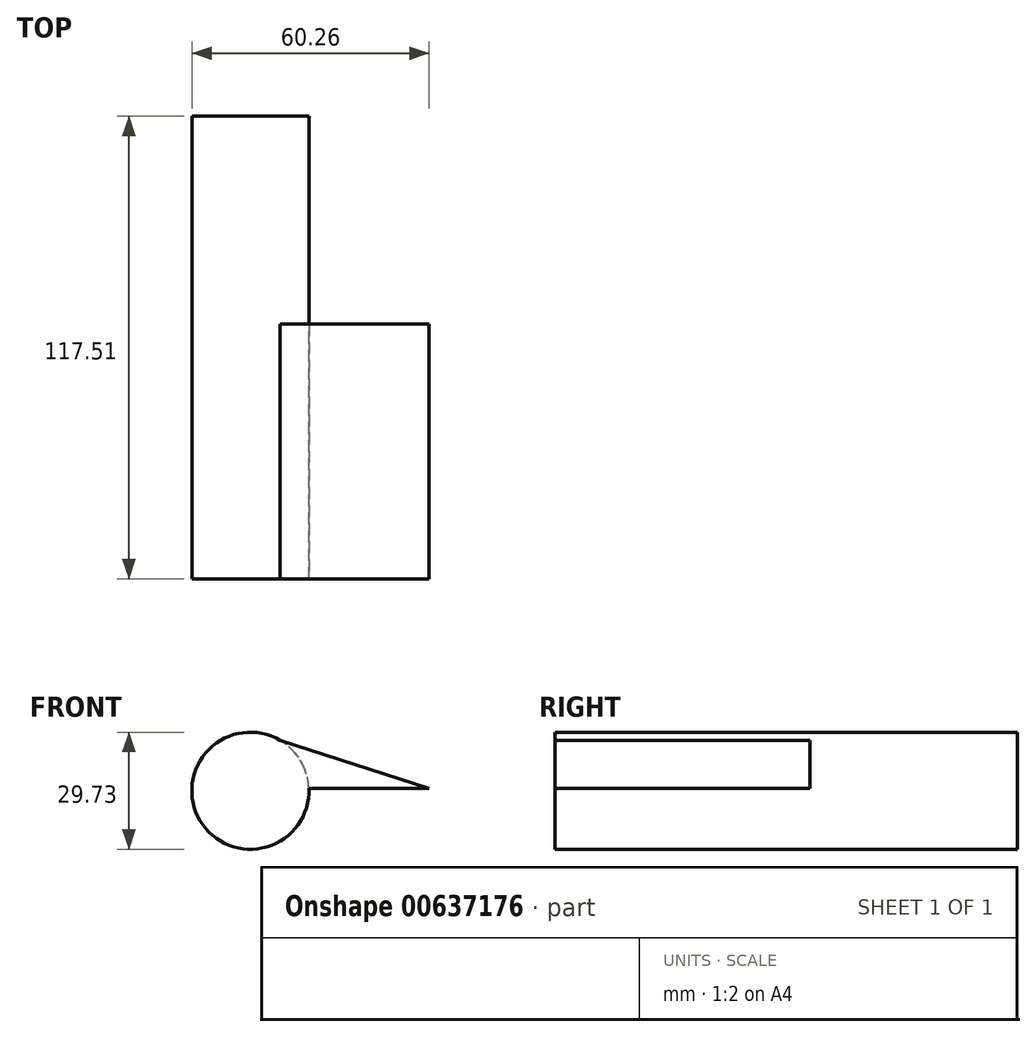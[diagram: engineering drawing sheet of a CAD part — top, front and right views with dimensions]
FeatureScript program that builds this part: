
annotation { "Feature Type Name" : "Feature", "Feature Type Description" : "" }
export const myFeature = defineFeature(function(context is Context, id is Id, definition is map)
    precondition{}
    {
        {
            var Q0;
            Q0=qCreatedBy(makeId("Front.planeOp"),FACE);
            var sketch = newSketch(context, id + "F0", { "sketchPlane" : qUnion([Q0])});
            skCircle(sketch, "E0", {"center": v(-0.34, -0.59) * mm, "radius": 14.87 * mm});
            skPoint(sketch, "E0.first.point", {"position": v(14.51, 0) * mm});
            skPoint(sketch, "E0.second.point", {"position": v(-15.2, 0) * mm});
            skPoint(sketch, "E0.third.point", {"position": v(0, 14.28) * mm});
            skSolve(sketch);
        }
        {
            var Q0;
            Q0=makeQuery(id+"F0.imprint","IMPRINT",FACE,{"disambiguationData":[TD([[makeQuery(id+"F0.imprint","IMPRINT",EDGE,{"derivedFrom":sQuery(id+"F0.wireOp",EDGE,"E0")}),1.0]])]});
            extrude(context, id + "F1", {"entities" : qUnion([Q0]), "depth" : 63.81 * mm, "offsetDistance" : 25.4 * mm});
        }
        {
            var Q0;
            Q0=makeQuery(id+"F1.opExtrude","CAP_FACE",FACE,{"disambiguationData":[OSD([sQuery(id+"F0.wireOp",EDGE,"E0")])],"isStart":true});
            extrude(context, id + "F2", {"entities" : qUnion([Q0]), "operationType" : NewBodyOperationType.ADD, "depth" : 53.7 * mm, "offsetDistance" : 25.4 * mm});
        }
        {
            var Q0;
            Q0=makeQuery(id+"F1.opExtrude","CAP_FACE",FACE,{"disambiguationData":[OSD([sQuery(id+"F0.wireOp",EDGE,"E0")])],"isStart":false});
            var sketch = newSketch(context, id + "F3", { "sketchPlane" : qUnion([Q0])});
            skLineSegment(sketch, "E1", {"start": v(14.51, 0) * mm, "end": v(45.05, 0) * mm});
            skLineSegment(sketch, "E2", {"start": v(45.05, 0) * mm, "end": v(7.23, 12.2) * mm});
            skSolve(sketch);
        }
        {
            var Q0;
            {var subQ0=sQuery(id+"F3.wireOp",EDGE,"E1");Q0=makeQuery(id+"F3.imprint","IMPRINT",FACE,{"disambiguationData":[TD([[makeQuery(id+"F3.imprint","IMPRINT",EDGE,{"derivedFrom":subQ0}),1.0]])]});}
            extrude(context, id + "F4", {"entities" : qUnion([Q0]), "operationType" : NewBodyOperationType.ADD, "oppositeDirection" : true, "depth" : 64.72 * mm, "offsetDistance" : 25.4 * mm});
        }
    });
